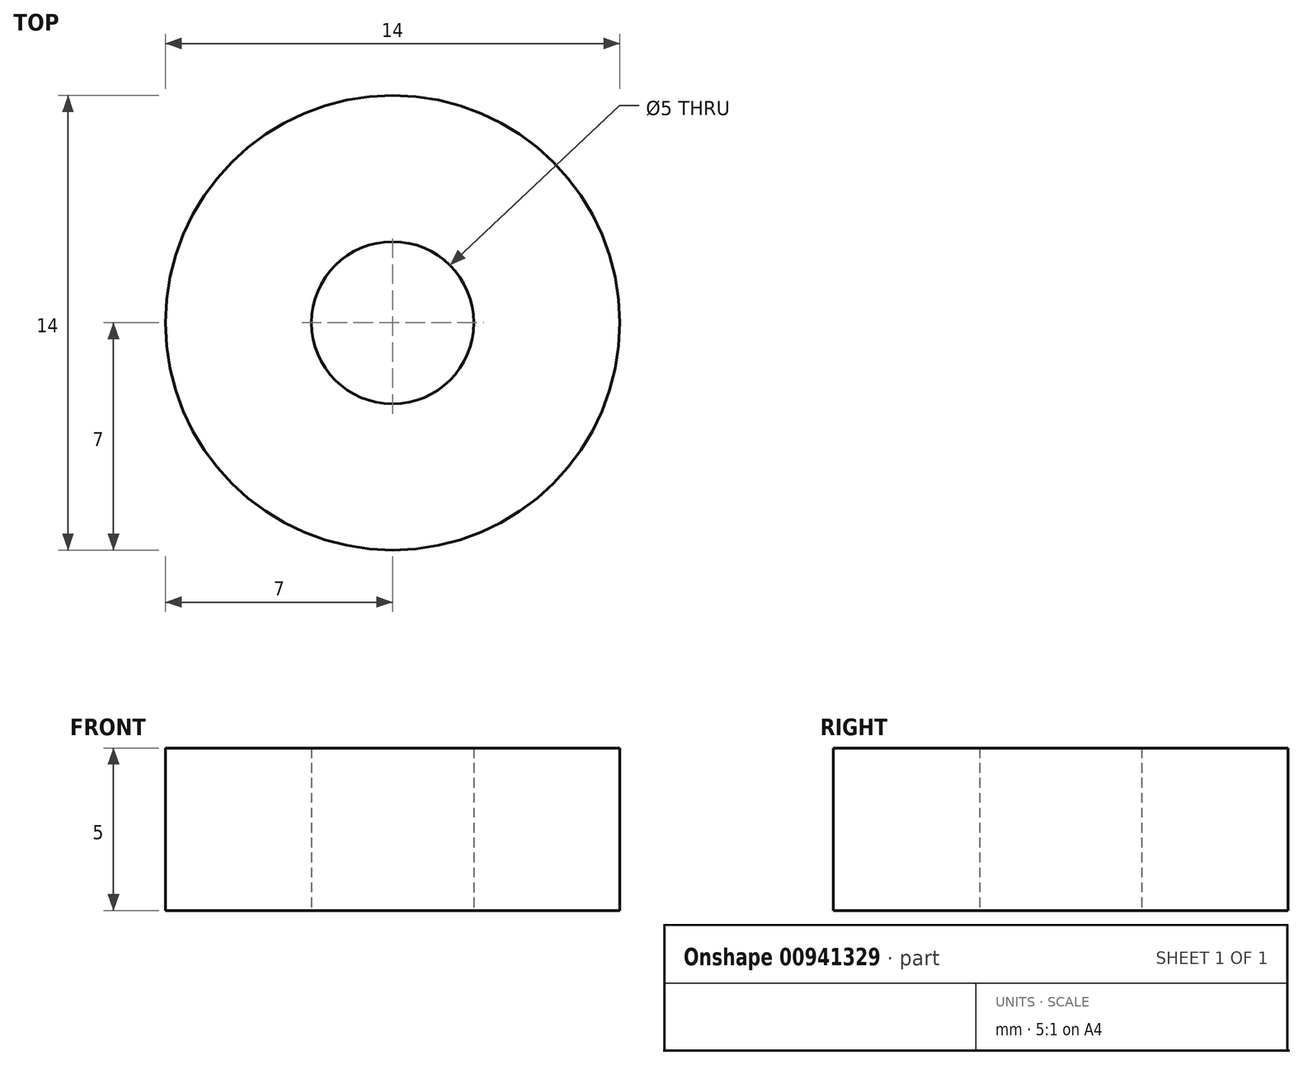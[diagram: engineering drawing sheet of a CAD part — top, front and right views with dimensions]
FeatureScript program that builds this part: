
annotation { "Feature Type Name" : "Feature", "Feature Type Description" : "" }
export const myFeature = defineFeature(function(context is Context, id is Id, definition is map)
    precondition{}
    {
        {
            var Q0;
            Q0=qCreatedBy(makeId("Top.planeOp"),FACE);
            var sketch = newSketch(context, id + "F0", { "sketchPlane" : qUnion([Q0])});
            skCircle(sketch, "E0", {"center": v(0, 0) * mm, "radius": 2.5 * mm});
            skCircle(sketch, "E1", {"center": v(0, 0) * mm, "radius": 7 * mm});
            skSolve(sketch);
        }
        {
            var Q0;
            Q0=makeQuery(id+"F0.imprint","IMPRINT",FACE,{"disambiguationData":[TD([[makeQuery(id+"F0.imprint","IMPRINT",EDGE,{"derivedFrom":sQuery(id+"F0.wireOp",EDGE,"E0")}),-1.0]])]});
            extrude(context, id + "F1", {"entities" : qUnion([Q0]), "depth" : 5 * mm, "offsetDistance" : 25 * mm});
        }
    });
